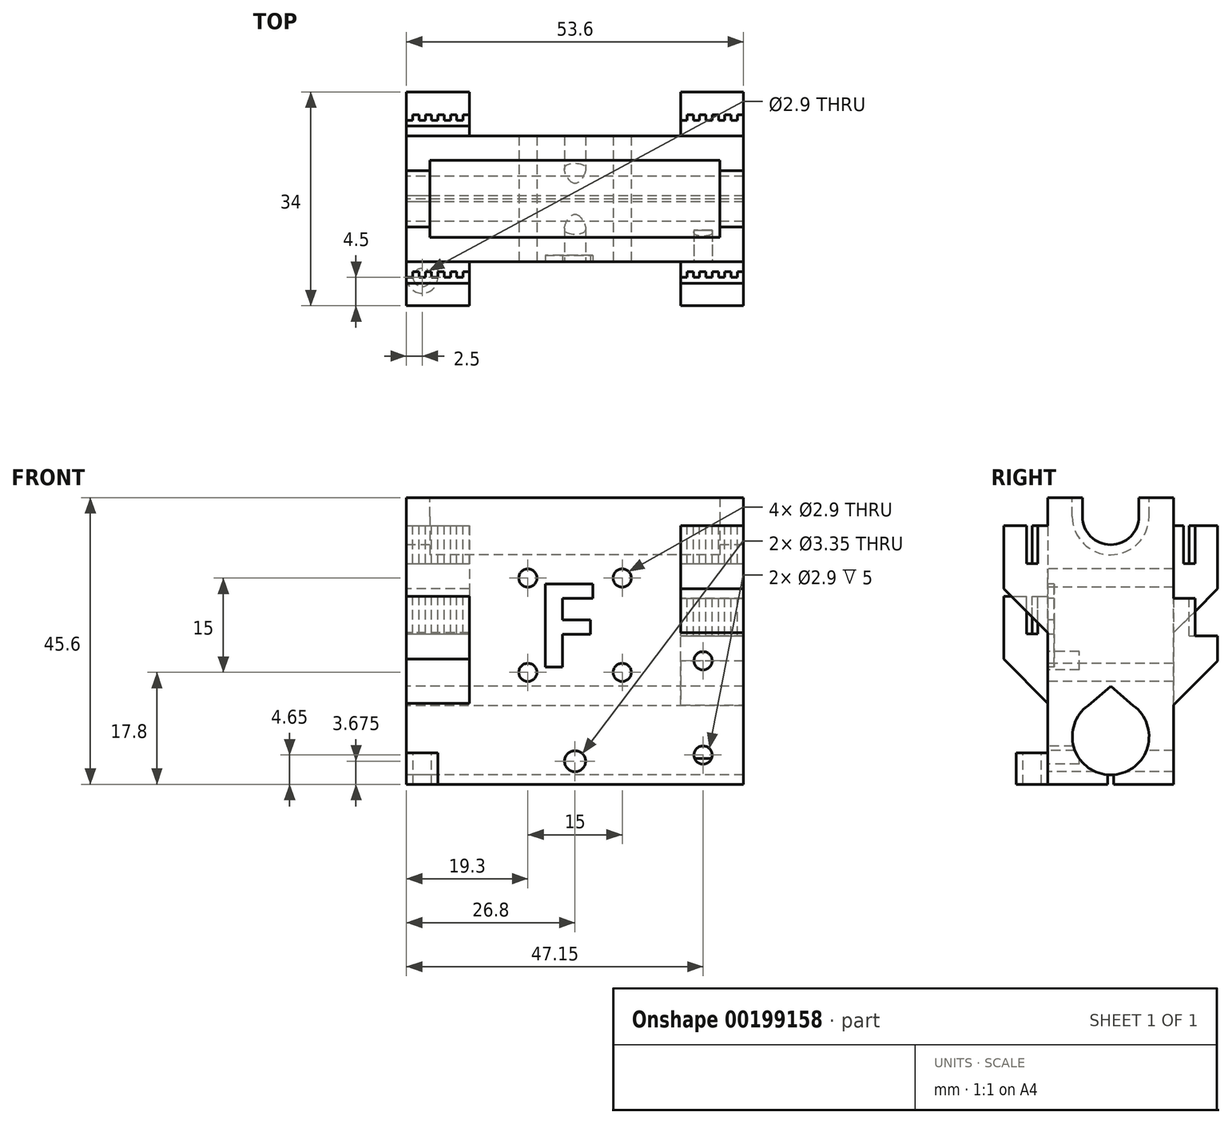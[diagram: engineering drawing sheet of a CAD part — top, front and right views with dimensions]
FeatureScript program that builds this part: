
annotation { "Feature Type Name" : "Feature", "Feature Type Description" : "" }
export const myFeature = defineFeature(function(context is Context, id is Id, definition is map)
    precondition{}
    {
        {
            assignVariable(context, id + "F0", {"name" : "LM8LUU", "anyValue" : 1.8});
        }
        {
            var Q0;
            Q0=qCreatedBy(makeId("Top.planeOp"),FACE);
            var sketch = newSketch(context, id + "F1", { "sketchPlane" : qUnion([Q0])});
            skLineSegment(sketch, "E0.bottom", {"start": v(0, 0) * mm, "end": v(53.6, 0) * mm});
            skLineSegment(sketch, "E0.top", {"start": v(0, 20) * mm, "end": v(53.6, 20) * mm});
            skLineSegment(sketch, "E0.left", {"start": v(0, 0) * mm, "end": v(0, 20) * mm});
            skLineSegment(sketch, "E0.right", {"start": v(53.6, 0) * mm, "end": v(53.6, 20) * mm});
            skSolve(sketch);
        }
        {
            var Q0;
            Q0=qSketchRegion(id+"F1",true);
            extrude(context, id + "F2", {"entities" : qUnion([Q0]), "depth" : 50.6 * mm});
        }
        {
            var Q0;
            {var subQ0=sQuery(id+"F5.wireOp",EDGE,"b7c4184e-802c-4243-a026-41b5801e035c");var subQ1=sQuery(id+"F5.wireOp",EDGE,"2d033815-d19a-4ada-85c1-b424e2f57677");var subQ2=sQuery(id+"F5.wireOp",EDGE,"E15");var subQ3=sQuery(id+"F5.wireOp",EDGE,"deb4647e-459a-4bd0-b85b-410e59fd364d");var subQ4=sQuery(id+"F5.wireOp",EDGE,"1f1fe5f8-645c-480d-a2d4-7acea15178eb");var subQ5=sQuery(id+"F5.wireOp",EDGE,"E4");var subQ6=sQuery(id+"F1.wireOp",EDGE,"E0.left");Q0=makeQuery(id+"F32.boolean.opBoolean","MERGE",FACE,{"derivedFrom":[makeQuery(id+"F19.boolean.opBoolean","MERGE",FACE,{"derivedFrom":[makeQuery(id+"F12.boolean.opBoolean","MERGE",FACE,{"derivedFrom":[makeQuery(id+"F10.boolean.opBoolean","MERGE",FACE,{"derivedFrom":[makeQuery(id+"F8.boolean.opBoolean","MERGE",FACE,{"derivedFrom":[makeQuery(id+"F2.opExtrude","SWEPT_FACE",FACE,{"disambiguationData":[OSD([subQ6])]}),makeQuery(id+"F8.opExtrude","CAP_FACE",FACE,{"disambiguationData":[OSD([subQ6,subQ5,subQ4,subQ3,subQ2,subQ1,subQ0])],"isStart":true})]}),makeQuery(id+"F10.opExtrude","CAP_FACE",FACE,{"disambiguationData":[OSD([subQ6,subQ5,subQ4,subQ3,subQ2,subQ1,subQ0])],"isStart":true})]}),makeQuery(id+"F12.opExtrude","SWEPT_FACE",FACE,{"disambiguationData":[OSD([sQuery(id+"F11.wireOp",EDGE,"E20.left")])]})]}),makeQuery(id+"F19.opExtrude","SWEPT_FACE",FACE,{"disambiguationData":[OSD([sQuery(id+"F18.wireOp",EDGE,"E76.left")])]})]}),makeQuery(id+"F32.opExtrude","SWEPT_FACE",FACE,{"disambiguationData":[OSD([sQuery(id+"F31.wireOp",EDGE,"E147.left")])]})]});}
            var sketch = newSketch(context, id + "F3", { "sketchPlane" : qUnion([Q0])});
            skPoint(sketch, "E1", {"position": v(-20, 45.6) * mm});
            skLineSegment(sketch, "E2.bottom", {"start": v(-20, 45.6) * mm, "end": v(0, 45.6) * mm});
            skLineSegment(sketch, "E2.top", {"start": v(-20, 50.6) * mm, "end": v(0, 50.6) * mm});
            skLineSegment(sketch, "E2.left", {"start": v(-20, 45.6) * mm, "end": v(-20, 50.6) * mm});
            skLineSegment(sketch, "E2.right", {"start": v(0, 45.6) * mm, "end": v(0, 50.6) * mm});
            skSolve(sketch);
        }
        {
            var Q0;
            Q0 = qSketchRegion(id + "F3", true);
            extrude(context, id + "F4", {"entities" : qUnion([Q0]), "operationType" : NewBodyOperationType.REMOVE, "endBound" : BoundingType.THROUGH_ALL, "oppositeDirection" : true, "depth" : 25 * mm});
        }
        {
            var Q0;
            Q0=makeQuery(id+"F2.opExtrude","SWEPT_FACE",FACE,{"disambiguationData":[OSD([sQuery(id+"F1.wireOp",EDGE,"E0.left")])]});
            var sketch = newSketch(context, id + "F5", { "sketchPlane" : qUnion([Q0])});
            skCircle(sketch, "E3", {"center": v(-10, 7.6) * mm, "radius": 6.1 * mm});
            skCircle(sketch, "E4", {"center": v(-10, 42.6) * mm, "radius": 4.5 * mm});
            skLineSegment(sketch, "E5", {"start": v(-20, 7.6) * mm, "end": v(0, 7.6) * mm, "construction": true});
            skLineSegment(sketch, "E6", {"start": v(-10, 7.6) * mm, "end": v(-10, 0) * mm, "construction": true});
            skLineSegment(sketch, "E7", {"start": v(-10, 0) * mm, "end": v(-10.5, 0) * mm});
            skLineSegment(sketch, "E8", {"start": v(-10.5, 0) * mm, "end": v(-10.5, 1.52) * mm});
            skLineSegment(sketch, "E9", {"start": v(-10.5, 1.52) * mm, "end": v(-9.5, 1.52) * mm});
            skLineSegment(sketch, "E10", {"start": v(-9.5, 1.52) * mm, "end": v(-9.5, 0) * mm});
            skLineSegment(sketch, "E11", {"start": v(-9.5, 0) * mm, "end": v(-10, 0) * mm});
            skLineSegment(sketch, "E12", {"start": v(-10, 13.7) * mm, "end": v(-10, 15.6) * mm});
            skLineSegment(sketch, "E13", {"start": v(-10, 15.6) * mm, "end": v(-6.39, 12.51) * mm});
            skLineSegment(sketch, "E14", {"start": v(-10, 15.6) * mm, "end": v(-13.61, 12.51) * mm});
            skCircle(sketch, "E15", {"center": v(-10, 42.6) * mm, "radius": 6.1 * mm});
            skLineSegment(sketch, "E16", {"start": v(-14.5, 42.6) * mm, "end": v(-14.5, 45.6) * mm});
            skLineSegment(sketch, "E17", {"start": v(-16.1, 42.6) * mm, "end": v(-16.1, 45.6) * mm});
            skLineSegment(sketch, "E18", {"start": v(-5.5, 42.6) * mm, "end": v(-5.5, 45.6) * mm});
            skLineSegment(sketch, "E19", {"start": v(-3.9, 42.6) * mm, "end": v(-3.9, 45.6) * mm});
            skSolve(sketch);
        }
        {
            var Q0;
            {var subQ0=sQuery(id+"F5.wireOp",EDGE,"E13");var subQ1=sQuery(id+"F5.wireOp",EDGE,"E3");var subQ3=makeQuery(id+"F5.imprint","INTERSECT",VERTEX,{"disambiguationData":[OD(0.0)],"derivedFrom":[subQ1,subQ0]});Q0=makeQuery(id+"F5.imprint","IMPRINT",FACE,{"disambiguationData":[TD([[makeQuery(id+"F5.imprint","IMPRINT",EDGE,{"disambiguationData":[TD([[subQ3,-1.0]])],"derivedFrom":subQ1}),1.0]])]});}
            var Q1;
            {var subQ0=sQuery(id+"F5.wireOp",EDGE,"E14");var subQ1=sQuery(id+"F5.wireOp",EDGE,"E3");var subQ3=makeQuery(id+"F5.imprint","INTERSECT",VERTEX,{"disambiguationData":[OD(0.0)],"derivedFrom":[subQ1,subQ0]});Q1=makeQuery(id+"F5.imprint","IMPRINT",FACE,{"disambiguationData":[TD([[makeQuery(id+"F5.imprint","IMPRINT",EDGE,{"disambiguationData":[TD([[subQ3,1.0]])],"derivedFrom":subQ1}),1.0]])]});}
            var Q2;
            Q2=makeQuery(id+"F5.imprint","IMPRINT",FACE,{"disambiguationData":[TD([[makeQuery(id+"F5.imprint","IMPRINT",EDGE,{"derivedFrom":sQuery(id+"F5.wireOp",EDGE,"E7")}),-1.0]])]});
            var Q3;
            {var subQ0=sQuery(id+"F5.wireOp",EDGE,"E9");Q3=makeQuery(id+"F5.imprint","IMPRINT",FACE,{"disambiguationData":[TD([[makeQuery(id+"F5.imprint","IMPRINT",EDGE,{"derivedFrom":subQ0}),-1.0]])]});}
            var Q4;
            {var subQ3=sQuery(id+"F5.wireOp",EDGE,"E12");Q4=makeQuery(id+"F5.imprint","IMPRINT",FACE,{"disambiguationData":[TD([[makeQuery(id+"F5.imprint","IMPRINT",EDGE,{"derivedFrom":subQ3}),-1.0]])]});}
            var Q5;
            {var subQ3=sQuery(id+"F5.wireOp",EDGE,"E12");Q5=makeQuery(id+"F5.imprint","IMPRINT",FACE,{"disambiguationData":[TD([[makeQuery(id+"F5.imprint","IMPRINT",EDGE,{"derivedFrom":subQ3}),1.0]])]});}
            var Q6;
            {var subQ7=sQuery(id+"F5.wireOp",EDGE,"E9");Q6=makeQuery(id+"F5.imprint","IMPRINT",FACE,{"disambiguationData":[TD([[makeQuery(id+"F5.imprint","IMPRINT",EDGE,{"derivedFrom":subQ7}),1.0]])]});}
            var Q7;
            {var subQ3=sQuery(id+"F5.wireOp",EDGE,"deb4647e-459a-4bd0-b85b-410e59fd364d");Q7=makeQuery(id+"F5.imprint","IMPRINT",FACE,{"disambiguationData":[TD([[makeQuery(id+"F5.imprint","IMPRINT",EDGE,{"derivedFrom":subQ3}),-1.0]])]});}
            var Q8;
            {var subQ0=sQuery(id+"F5.wireOp",EDGE,"1f1fe5f8-645c-480d-a2d4-7acea15178eb");Q8=makeQuery(id+"F5.imprint","IMPRINT",FACE,{"disambiguationData":[TD([[makeQuery(id+"F5.imprint","IMPRINT",EDGE,{"derivedFrom":subQ0}),1.0]])]});}
            var Q9;
            {var subQ0=sQuery(id+"F5.wireOp",EDGE,"1f1fe5f8-645c-480d-a2d4-7acea15178eb");Q9=makeQuery(id+"F5.imprint","IMPRINT",FACE,{"disambiguationData":[TD([[makeQuery(id+"F5.imprint","IMPRINT",EDGE,{"derivedFrom":subQ0}),1.0]])]});}
            var Q10;
            {var subQ3=sQuery(id+"F5.wireOp",EDGE,"deb4647e-459a-4bd0-b85b-410e59fd364d");Q10=makeQuery(id+"F5.imprint","IMPRINT",FACE,{"disambiguationData":[TD([[makeQuery(id+"F5.imprint","IMPRINT",EDGE,{"derivedFrom":subQ3}),-1.0]])]});}
            var Q11;
            {var subQ1=sQuery(id+"F5.wireOp",EDGE,"E4");var subQ4=makeQuery(id+"F5.imprint","INTERSECT",VERTEX,{"derivedFrom":[subQ1,sQuery(id+"F5.wireOp",EDGE,"deb4647e-459a-4bd0-b85b-410e59fd364d")]});Q11=makeQuery(id+"F5.imprint","IMPRINT",FACE,{"disambiguationData":[TD([[makeQuery(id+"F5.imprint","IMPRINT",EDGE,{"disambiguationData":[TD([[subQ4,-1.0]])],"derivedFrom":subQ1}),1.0]])]});}
            var Q12;
            {var subQ0=sQuery(id+"F5.wireOp",EDGE,"E18");Q12=makeQuery(id+"F5.imprint","IMPRINT",FACE,{"disambiguationData":[TD([[makeQuery(id+"F5.imprint","IMPRINT",EDGE,{"derivedFrom":subQ0}),1.0]])]});}
            var Q13;
            {var subQ0=sQuery(id+"F5.wireOp",EDGE,"E16");Q13=makeQuery(id+"F5.imprint","IMPRINT",FACE,{"disambiguationData":[TD([[makeQuery(id+"F5.imprint","IMPRINT",EDGE,{"derivedFrom":subQ0}),-1.0]])]});}
            extrude(context, id + "F6", {"entities" : qUnion([Q0, Q1, Q2, Q3, Q4, Q5, Q6, Q7, Q8, Q9, Q10, Q11, Q12, Q13]), "operationType" : NewBodyOperationType.REMOVE, "endBound" : BoundingType.THROUGH_ALL, "oppositeDirection" : true, "depth" : 25 * mm});
        }
        {
            var Q0;
            {var subQ0=sQuery(id+"F5.wireOp",EDGE,"E9");Q0=makeQuery(id+"F5.imprint","IMPRINT",FACE,{"disambiguationData":[TD([[makeQuery(id+"F5.imprint","IMPRINT",EDGE,{"derivedFrom":subQ0}),-1.0]])]});}
            var Q1;
            {var subQ0=sQuery(id+"F5.wireOp",EDGE,"E18");Q1=makeQuery(id+"F5.imprint","IMPRINT",FACE,{"disambiguationData":[TD([[makeQuery(id+"F5.imprint","IMPRINT",EDGE,{"derivedFrom":subQ0}),1.0]])]});}
            var Q2;
            {var subQ0=sQuery(id+"F5.wireOp",EDGE,"E16");Q2=makeQuery(id+"F5.imprint","IMPRINT",FACE,{"disambiguationData":[TD([[makeQuery(id+"F5.imprint","IMPRINT",EDGE,{"derivedFrom":subQ0}),-1.0]])]});}
            var Q3;
            {var subQ6=sQuery(id+"F5.wireOp",EDGE,"E16");Q3=makeQuery(id+"F5.imprint","IMPRINT",FACE,{"disambiguationData":[TD([[makeQuery(id+"F5.imprint","IMPRINT",EDGE,{"derivedFrom":subQ6}),1.0]])]});}
            var Q4;
            {var subQ0=makeQuery(id+"F4.boolean.opBoolean","COPY",EDGE,{"derivedFrom":makeQuery(id+"F4.opExtrude","CAP_EDGE",EDGE,{"disambiguationData":[OSD([sQuery(id+"F3.wireOp",EDGE,"E2.bottom")])],"isStart":true})});var subQ2=sQuery(id+"F5.wireOp",EDGE,"E4");var subQ8=makeQuery(id+"F5.imprint","INTERSECT",VERTEX,{"disambiguationData":[OD(0.0)],"derivedFrom":[subQ0,subQ2]});Q4=makeQuery(id+"F5.imprint","IMPRINT",FACE,{"disambiguationData":[TD([[makeQuery(id+"F5.imprint","IMPRINT",EDGE,{"disambiguationData":[TD([[subQ8,-1.0]])],"derivedFrom":subQ2}),-1.0]])]});}
            var Q5;
            {var subQ0=sQuery(id+"F5.wireOp",EDGE,"E19");Q5=makeQuery(id+"F5.imprint","IMPRINT",FACE,{"disambiguationData":[TD([[makeQuery(id+"F5.imprint","IMPRINT",EDGE,{"derivedFrom":subQ0}),1.0]])]});}
            var Q6;
            {var subQ0=sQuery(id+"F5.wireOp",EDGE,"E17");Q6=makeQuery(id+"F5.imprint","IMPRINT",FACE,{"disambiguationData":[TD([[makeQuery(id+"F5.imprint","IMPRINT",EDGE,{"derivedFrom":subQ0}),-1.0]])]});}
            extrude(context, id + "F7", {"entities" : qUnion([Q0, Q1, Q2, Q3, Q4, Q5, Q6]), "operationType" : NewBodyOperationType.REMOVE, "oppositeDirection" : true, "depth" : (46.25 + getVariable(context, 'LM8LUU') * 2) * mm});
        }
        {
            var Q0;
            {var subQ0=sQuery(id+"F5.wireOp",EDGE,"E9");Q0=makeQuery(id+"F5.imprint","IMPRINT",FACE,{"disambiguationData":[TD([[makeQuery(id+"F5.imprint","IMPRINT",EDGE,{"derivedFrom":subQ0}),-1.0]])]});}
            var Q1;
            {var subQ6=sQuery(id+"F5.wireOp",EDGE,"E16");Q1=makeQuery(id+"F5.imprint","IMPRINT",FACE,{"disambiguationData":[TD([[makeQuery(id+"F5.imprint","IMPRINT",EDGE,{"derivedFrom":subQ6}),1.0]])]});}
            var Q2;
            {var subQ0=sQuery(id+"F5.wireOp",EDGE,"E17");Q2=makeQuery(id+"F5.imprint","IMPRINT",FACE,{"disambiguationData":[TD([[makeQuery(id+"F5.imprint","IMPRINT",EDGE,{"derivedFrom":subQ0}),-1.0]])]});}
            var Q3;
            {var subQ0=sQuery(id+"F5.wireOp",EDGE,"E19");Q3=makeQuery(id+"F5.imprint","IMPRINT",FACE,{"disambiguationData":[TD([[makeQuery(id+"F5.imprint","IMPRINT",EDGE,{"derivedFrom":subQ0}),1.0]])]});}
            extrude(context, id + "F8", {"entities" : qUnion([Q0, Q1, Q2, Q3]), "operationType" : NewBodyOperationType.ADD, "oppositeDirection" : true, "depth" : (26.75 - getVariable(context, 'LM8LUU')) * mm});
        }
        {
            var Q0;
            Q0=makeQuery(id+"F5.imprint","IMPRINT",FACE,{"disambiguationData":[TD([[makeQuery(id+"F5.imprint","IMPRINT",EDGE,{"derivedFrom":sQuery(id+"F5.wireOp",EDGE,"E7")}),-1.0]])]});
            var Q1;
            {var subQ0=sQuery(id+"F5.wireOp",EDGE,"E9");Q1=makeQuery(id+"F5.imprint","IMPRINT",FACE,{"disambiguationData":[TD([[makeQuery(id+"F5.imprint","IMPRINT",EDGE,{"derivedFrom":subQ0}),-1.0]])]});}
            var Q2;
            {var subQ0=sQuery(id+"F5.wireOp",EDGE,"E12");Q2=makeQuery(id+"F5.imprint","IMPRINT",FACE,{"disambiguationData":[TD([[makeQuery(id+"F5.imprint","IMPRINT",EDGE,{"derivedFrom":subQ0}),-1.0]])]});}
            var Q3;
            {var subQ0=sQuery(id+"F5.wireOp",EDGE,"E12");Q3=makeQuery(id+"F5.imprint","IMPRINT",FACE,{"disambiguationData":[TD([[makeQuery(id+"F5.imprint","IMPRINT",EDGE,{"derivedFrom":subQ0}),1.0]])]});}
            var Q4;
            {var subQ3=sQuery(id+"F5.wireOp",EDGE,"E9");Q4=makeQuery(id+"F5.imprint","IMPRINT",FACE,{"disambiguationData":[TD([[makeQuery(id+"F5.imprint","IMPRINT",EDGE,{"derivedFrom":subQ3}),1.0]])]});}
            var Q5;
            {var subQ6=sQuery(id+"F5.wireOp",EDGE,"E16");Q5=makeQuery(id+"F5.imprint","IMPRINT",FACE,{"disambiguationData":[TD([[makeQuery(id+"F5.imprint","IMPRINT",EDGE,{"derivedFrom":subQ6}),1.0]])]});}
            var Q6;
            {var subQ0=sQuery(id+"F5.wireOp",EDGE,"E17");Q6=makeQuery(id+"F5.imprint","IMPRINT",FACE,{"disambiguationData":[TD([[makeQuery(id+"F5.imprint","IMPRINT",EDGE,{"derivedFrom":subQ0}),-1.0]])]});}
            var Q7;
            {var subQ0=sQuery(id+"F5.wireOp",EDGE,"E19");Q7=makeQuery(id+"F5.imprint","IMPRINT",FACE,{"disambiguationData":[TD([[makeQuery(id+"F5.imprint","IMPRINT",EDGE,{"derivedFrom":subQ0}),1.0]])]});}
            extrude(context, id + "F9", {"entities" : qUnion([Q0, Q1, Q2, Q3, Q4, Q5, Q6, Q7]), "operationType" : NewBodyOperationType.REMOVE, "oppositeDirection" : true, "depth" : (23.25 + getVariable(context, 'LM8LUU')) * mm});
        }
        {
            var Q0;
            {var subQ0=sQuery(id+"F5.wireOp",EDGE,"E9");Q0=makeQuery(id+"F5.imprint","IMPRINT",FACE,{"disambiguationData":[TD([[makeQuery(id+"F5.imprint","IMPRINT",EDGE,{"derivedFrom":subQ0}),-1.0]])]});}
            var Q1;
            {var subQ6=sQuery(id+"F5.wireOp",EDGE,"E16");Q1=makeQuery(id+"F5.imprint","IMPRINT",FACE,{"disambiguationData":[TD([[makeQuery(id+"F5.imprint","IMPRINT",EDGE,{"derivedFrom":subQ6}),1.0]])]});}
            var Q2;
            {var subQ0=sQuery(id+"F5.wireOp",EDGE,"E17");Q2=makeQuery(id+"F5.imprint","IMPRINT",FACE,{"disambiguationData":[TD([[makeQuery(id+"F5.imprint","IMPRINT",EDGE,{"derivedFrom":subQ0}),-1.0]])]});}
            var Q3;
            {var subQ0=sQuery(id+"F5.wireOp",EDGE,"E19");Q3=makeQuery(id+"F5.imprint","IMPRINT",FACE,{"disambiguationData":[TD([[makeQuery(id+"F5.imprint","IMPRINT",EDGE,{"derivedFrom":subQ0}),1.0]])]});}
            extrude(context, id + "F10", {"entities" : qUnion([Q0, Q1, Q2, Q3]), "operationType" : NewBodyOperationType.ADD, "oppositeDirection" : true, "depth" : 3.75 * mm});
        }
        {
            var Q0;
            Q0=makeQuery(id+"F2.opExtrude","SWEPT_FACE",FACE,{"disambiguationData":[OSD([sQuery(id+"F1.wireOp",EDGE,"E0.bottom")])]});
            var sketch = newSketch(context, id + "F11", { "sketchPlane" : qUnion([Q0])});
            skLineSegment(sketch, "E20.bottom", {"start": v(0, 29.9) * mm, "end": v(10, 29.9) * mm});
            skLineSegment(sketch, "E20.top", {"start": v(0, 9.9) * mm, "end": v(10, 9.9) * mm});
            skLineSegment(sketch, "E20.left", {"start": v(0, 29.9) * mm, "end": v(0, 9.9) * mm});
            skLineSegment(sketch, "E20.right", {"start": v(10, 29.9) * mm, "end": v(10, 9.9) * mm});
            skLineSegment(sketch, "E21.bottom", {"start": v(53.6, 41.1) * mm, "end": v(43.6, 41.1) * mm});
            skLineSegment(sketch, "E21.top", {"start": v(53.6, 21.1) * mm, "end": v(43.6, 21.1) * mm});
            skLineSegment(sketch, "E21.left", {"start": v(53.6, 41.1) * mm, "end": v(53.6, 21.1) * mm});
            skLineSegment(sketch, "E21.right", {"start": v(43.6, 41.1) * mm, "end": v(43.6, 21.1) * mm});
            skPoint(sketch, "E22", {"position": v(0, 47.6) * mm});
            skPoint(sketch, "E23", {"position": v(0, 9.4) * mm});
            skSolve(sketch);
        }
        {
            var Q0;
            Q0=qSketchRegion(id+"F11",true);
            extrude(context, id + "F12", {"entities" : qUnion([Q0]), "operationType" : NewBodyOperationType.ADD, "depth" : 7 * mm});
        }
        {
            var Q0;
            Q0=makeQuery(id+"F12.opExtrude","CAP_EDGE",EDGE,{"disambiguationData":[OSD([sQuery(id+"F11.wireOp",EDGE,"E20.top")])],"isStart":false});
            var Q1;
            Q1=makeQuery(id+"F12.opExtrude","CAP_EDGE",EDGE,{"disambiguationData":[OSD([sQuery(id+"F11.wireOp",EDGE,"E21.top")])],"isStart":false});
            chamfer(context, id + "F13", {"entities" : qUnion([Q0, Q1]), "width" : 10 * mm, "tangentPropagation" : true});
        }
        {
            var Q0;
            Q0=makeQuery(id+"F12.opExtrude","SWEPT_FACE",FACE,{"disambiguationData":[OSD([sQuery(id+"F11.wireOp",EDGE,"E20.bottom")])]});
            var sketch = newSketch(context, id + "F14", { "sketchPlane" : qUnion([Q0])});
            skLineSegment(sketch, "E24", {"start": v(-935.9, 0) * mm, "end": v(-935.88, -4.54) * mm});
            skLineSegment(sketch, "E25.left", {"start": v(0, -3.4) * mm, "end": v(0, -1.6) * mm});
            skLineSegment(sketch, "E26", {"start": v(6, -2.5) * mm, "end": v(7, -2.5) * mm});
            skLineSegment(sketch, "E27", {"start": v(4, -2.5) * mm, "end": v(5, -2.5) * mm});
            skLineSegment(sketch, "E28", {"start": v(0, -2.5) * mm, "end": v(1, -2.5) * mm});
            skLineSegment(sketch, "E29", {"start": v(7, -1.6) * mm, "end": v(8, -1.6) * mm});
            skLineSegment(sketch, "E30", {"start": v(2, -2.5) * mm, "end": v(3, -2.5) * mm});
            skLineSegment(sketch, "E31", {"start": v(3, -1.6) * mm, "end": v(4, -1.6) * mm});
            skLineSegment(sketch, "E32", {"start": v(8, -2.5) * mm, "end": v(9, -2.5) * mm});
            skLineSegment(sketch, "E33", {"start": v(8, -1.6) * mm, "end": v(8, -2.5) * mm});
            skLineSegment(sketch, "E34", {"start": v(9, -2.5) * mm, "end": v(9, -1.6) * mm});
            skLineSegment(sketch, "E35", {"start": v(10, -1.6) * mm, "end": v(10, -2.5) * mm});
            skLineSegment(sketch, "E36", {"start": v(6, -1.6) * mm, "end": v(6, -2.5) * mm});
            skLineSegment(sketch, "E37", {"start": v(2, -1.6) * mm, "end": v(2, -2.5) * mm});
            skLineSegment(sketch, "E38", {"start": v(1, -1.6) * mm, "end": v(2, -1.6) * mm});
            skLineSegment(sketch, "E39", {"start": v(1, -2.5) * mm, "end": v(1, -1.6) * mm});
            skLineSegment(sketch, "E40", {"start": v(9, -1.6) * mm, "end": v(10, -1.6) * mm});
            skLineSegment(sketch, "E41", {"start": v(5, -1.6) * mm, "end": v(6, -1.6) * mm});
            skLineSegment(sketch, "E42", {"start": v(5, -2.5) * mm, "end": v(5, -1.6) * mm});
            skLineSegment(sketch, "E43", {"start": v(3, -2.5) * mm, "end": v(3, -1.6) * mm});
            skLineSegment(sketch, "E44", {"start": v(4, -1.6) * mm, "end": v(4, -2.5) * mm});
            skLineSegment(sketch, "E45", {"start": v(7, -2.5) * mm, "end": v(7, -1.6) * mm});
            skLineSegment(sketch, "E46", {"start": v(0, -1.6) * mm, "end": v(0, -2.5) * mm});
            skLineSegment(sketch, "E47", {"start": v(10, -2.5) * mm, "end": v(10, -3.4) * mm});
            skLineSegment(sketch, "E48", {"start": v(0, -3.4) * mm, "end": v(10, -3.4) * mm});
            skLineSegment(sketch, "E49", {"start": v(5.3, -1.6) * mm, "end": v(5.3, 0) * mm});
            skSolve(sketch);
        }
        {
            var Q0;
            Q0=qSketchRegion(id+"F14",true);
            extrude(context, id + "F15", {"entities" : qUnion([Q0]), "operationType" : NewBodyOperationType.REMOVE, "oppositeDirection" : true, "depth" : 6 * mm});
        }
        {
            var Q0;
            Q0=makeQuery(id+"F12.opExtrude","SWEPT_FACE",FACE,{"disambiguationData":[OSD([sQuery(id+"F11.wireOp",EDGE,"E21.bottom")])]});
            var sketch = newSketch(context, id + "F16", { "sketchPlane" : qUnion([Q0])});
            skLineSegment(sketch, "E50.left", {"start": v(43.6, -3.4) * mm, "end": v(43.6, -1.6) * mm});
            skLineSegment(sketch, "E51", {"start": v(49.6, -2.5) * mm, "end": v(50.6, -2.5) * mm});
            skLineSegment(sketch, "E52", {"start": v(47.6, -2.5) * mm, "end": v(48.6, -2.5) * mm});
            skLineSegment(sketch, "E53", {"start": v(43.6, -2.5) * mm, "end": v(44.6, -2.5) * mm});
            skLineSegment(sketch, "E54", {"start": v(50.6, -1.6) * mm, "end": v(51.6, -1.6) * mm});
            skLineSegment(sketch, "E55", {"start": v(45.6, -2.5) * mm, "end": v(46.6, -2.5) * mm});
            skLineSegment(sketch, "E56", {"start": v(46.6, -1.6) * mm, "end": v(47.6, -1.6) * mm});
            skLineSegment(sketch, "E57", {"start": v(51.6, -2.5) * mm, "end": v(52.6, -2.5) * mm});
            skLineSegment(sketch, "E58", {"start": v(51.6, -1.6) * mm, "end": v(51.6, -2.5) * mm});
            skLineSegment(sketch, "E59", {"start": v(52.6, -2.5) * mm, "end": v(52.6, -1.6) * mm});
            skLineSegment(sketch, "E60", {"start": v(53.6, -1.6) * mm, "end": v(53.6, -2.5) * mm});
            skLineSegment(sketch, "E61", {"start": v(49.6, -1.6) * mm, "end": v(49.6, -2.5) * mm});
            skLineSegment(sketch, "E62", {"start": v(45.6, -1.6) * mm, "end": v(45.6, -2.5) * mm});
            skLineSegment(sketch, "E63", {"start": v(44.6, -1.6) * mm, "end": v(45.6, -1.6) * mm});
            skLineSegment(sketch, "E64", {"start": v(44.6, -2.5) * mm, "end": v(44.6, -1.6) * mm});
            skLineSegment(sketch, "E65", {"start": v(52.6, -1.6) * mm, "end": v(53.6, -1.6) * mm});
            skLineSegment(sketch, "E66", {"start": v(48.6, -1.6) * mm, "end": v(49.6, -1.6) * mm});
            skLineSegment(sketch, "E67", {"start": v(48.6, -2.5) * mm, "end": v(48.6, -1.6) * mm});
            skLineSegment(sketch, "E68", {"start": v(46.6, -2.5) * mm, "end": v(46.6, -1.6) * mm});
            skLineSegment(sketch, "E69", {"start": v(47.6, -1.6) * mm, "end": v(47.6, -2.5) * mm});
            skLineSegment(sketch, "E70", {"start": v(50.6, -2.5) * mm, "end": v(50.6, -1.6) * mm});
            skLineSegment(sketch, "E71", {"start": v(43.6, -1.6) * mm, "end": v(43.6, -2.5) * mm});
            skLineSegment(sketch, "E72", {"start": v(53.6, -2.5) * mm, "end": v(53.6, -3.4) * mm});
            skLineSegment(sketch, "E73", {"start": v(43.6, -3.4) * mm, "end": v(53.6, -3.4) * mm});
            skLineSegment(sketch, "E74", {"start": v(48.83, -1.6) * mm, "end": v(48.83, 0) * mm});
            skSolve(sketch);
        }
        {
            var Q0;
            Q0=qSketchRegion(id+"F16",true);
            extrude(context, id + "F17", {"entities" : qUnion([Q0]), "operationType" : NewBodyOperationType.REMOVE, "oppositeDirection" : true, "depth" : 6 * mm});
        }
        {
            var Q0;
            Q0=makeQuery(id+"F2.opExtrude","SWEPT_FACE",FACE,{"disambiguationData":[OSD([sQuery(id+"F1.wireOp",EDGE,"E0.top")])]});
            var sketch = newSketch(context, id + "F18", { "sketchPlane" : qUnion([Q0])});
            skLineSegment(sketch, "E75.bottom", {"start": v(-53.6, 9.6) * mm, "end": v(-43.6, 9.6) * mm});
            skLineSegment(sketch, "E75.top", {"start": v(-53.6, 29.6) * mm, "end": v(-43.6, 29.6) * mm});
            skLineSegment(sketch, "E75.left", {"start": v(-53.6, 9.6) * mm, "end": v(-53.6, 29.6) * mm});
            skLineSegment(sketch, "E75.right", {"start": v(-43.6, 9.6) * mm, "end": v(-43.6, 29.6) * mm});
            skLineSegment(sketch, "E76.bottom", {"start": v(0, 41.1) * mm, "end": v(-10, 41.1) * mm});
            skLineSegment(sketch, "E76.top", {"start": v(0, 21.1) * mm, "end": v(-10, 21.1) * mm});
            skLineSegment(sketch, "E76.left", {"start": v(0, 41.1) * mm, "end": v(0, 21.1) * mm});
            skLineSegment(sketch, "E76.right", {"start": v(-10, 41.1) * mm, "end": v(-10, 21.1) * mm});
            skSolve(sketch);
        }
        {
            var Q0;
            Q0=qSketchRegion(id+"F18",true);
            extrude(context, id + "F19", {"entities" : qUnion([Q0]), "operationType" : NewBodyOperationType.ADD, "depth" : 7 * mm});
        }
        {
            var Q0;
            Q0=makeQuery(id+"F19.opExtrude","SWEPT_FACE",FACE,{"disambiguationData":[OSD([sQuery(id+"F18.wireOp",EDGE,"E75.top")])]});
            var sketch = newSketch(context, id + "F20", { "sketchPlane" : qUnion([Q0])});
            skLineSegment(sketch, "E77.left", {"start": v(43.6, 21.6) * mm, "end": v(43.6, 23.4) * mm});
            skLineSegment(sketch, "E78", {"start": v(49.6, 22.5) * mm, "end": v(50.6, 22.5) * mm});
            skLineSegment(sketch, "E79", {"start": v(47.6, 22.5) * mm, "end": v(48.6, 22.5) * mm});
            skLineSegment(sketch, "E80", {"start": v(43.6, 22.5) * mm, "end": v(44.6, 22.5) * mm});
            skLineSegment(sketch, "E81", {"start": v(50.6, 23.4) * mm, "end": v(51.6, 23.4) * mm});
            skLineSegment(sketch, "E82", {"start": v(45.6, 22.5) * mm, "end": v(46.6, 22.5) * mm});
            skLineSegment(sketch, "E83", {"start": v(46.6, 23.4) * mm, "end": v(47.6, 23.4) * mm});
            skLineSegment(sketch, "E84", {"start": v(51.6, 22.5) * mm, "end": v(52.6, 22.5) * mm});
            skLineSegment(sketch, "E85", {"start": v(51.6, 23.4) * mm, "end": v(51.6, 22.5) * mm});
            skLineSegment(sketch, "E86", {"start": v(52.6, 22.5) * mm, "end": v(52.6, 23.4) * mm});
            skLineSegment(sketch, "E87", {"start": v(53.6, 23.4) * mm, "end": v(53.6, 22.5) * mm});
            skLineSegment(sketch, "E88", {"start": v(49.6, 23.4) * mm, "end": v(49.6, 22.5) * mm});
            skLineSegment(sketch, "E89", {"start": v(45.6, 23.4) * mm, "end": v(45.6, 22.5) * mm});
            skLineSegment(sketch, "E90", {"start": v(44.6, 23.4) * mm, "end": v(45.6, 23.4) * mm});
            skLineSegment(sketch, "E91", {"start": v(44.6, 22.5) * mm, "end": v(44.6, 23.4) * mm});
            skLineSegment(sketch, "E92", {"start": v(52.6, 23.4) * mm, "end": v(53.6, 23.4) * mm});
            skLineSegment(sketch, "E93", {"start": v(48.6, 23.4) * mm, "end": v(49.6, 23.4) * mm});
            skLineSegment(sketch, "E94", {"start": v(48.6, 22.5) * mm, "end": v(48.6, 23.4) * mm});
            skLineSegment(sketch, "E95", {"start": v(46.6, 22.5) * mm, "end": v(46.6, 23.4) * mm});
            skLineSegment(sketch, "E96", {"start": v(47.6, 23.4) * mm, "end": v(47.6, 22.5) * mm});
            skLineSegment(sketch, "E97", {"start": v(50.6, 22.5) * mm, "end": v(50.6, 23.4) * mm});
            skLineSegment(sketch, "E98", {"start": v(43.6, 23.4) * mm, "end": v(43.6, 22.5) * mm});
            skLineSegment(sketch, "E99", {"start": v(53.6, 22.5) * mm, "end": v(53.6, 21.6) * mm});
            skLineSegment(sketch, "E100", {"start": v(43.6, 21.6) * mm, "end": v(53.6, 21.6) * mm});
            skLineSegment(sketch, "E101", {"start": v(48.6, 21.6) * mm, "end": v(48.6, 20) * mm});
            skSolve(sketch);
        }
        {
            var Q0;
            {var subQ4=sQuery(id+"F20.wireOp",EDGE,"E77.left");Q0=makeQuery(id+"F20.imprint","IMPRINT",FACE,{"disambiguationData":[TD([[makeQuery(id+"F20.imprint","IMPRINT",EDGE,{"derivedFrom":subQ4}),1.0]])]});}
            extrude(context, id + "F21", {"entities" : qUnion([Q0]), "operationType" : NewBodyOperationType.REMOVE, "oppositeDirection" : true, "depth" : 6 * mm});
        }
        {
            var Q0;
            Q0=makeQuery(id+"F19.opExtrude","SWEPT_FACE",FACE,{"disambiguationData":[OSD([sQuery(id+"F18.wireOp",EDGE,"E76.bottom")])]});
            var sketch = newSketch(context, id + "F22", { "sketchPlane" : qUnion([Q0])});
            skLineSegment(sketch, "E102", {"start": v(6, 22.5) * mm, "end": v(7, 22.5) * mm});
            skLineSegment(sketch, "E103", {"start": v(4, 22.5) * mm, "end": v(5, 22.5) * mm});
            skLineSegment(sketch, "E104", {"start": v(0, 22.5) * mm, "end": v(1, 22.5) * mm});
            skLineSegment(sketch, "E105", {"start": v(7, 23.4) * mm, "end": v(8, 23.4) * mm});
            skLineSegment(sketch, "E106", {"start": v(2, 22.5) * mm, "end": v(3, 22.5) * mm});
            skLineSegment(sketch, "E107", {"start": v(3, 23.4) * mm, "end": v(4, 23.4) * mm});
            skLineSegment(sketch, "E108", {"start": v(8, 22.5) * mm, "end": v(9, 22.5) * mm});
            skLineSegment(sketch, "E109", {"start": v(8, 23.4) * mm, "end": v(8, 22.5) * mm});
            skLineSegment(sketch, "E110", {"start": v(9, 22.5) * mm, "end": v(9, 23.4) * mm});
            skLineSegment(sketch, "E111", {"start": v(10, 23.4) * mm, "end": v(10, 22.5) * mm});
            skLineSegment(sketch, "E112", {"start": v(6, 23.4) * mm, "end": v(6, 22.5) * mm});
            skLineSegment(sketch, "E113", {"start": v(2, 23.4) * mm, "end": v(2, 22.5) * mm});
            skLineSegment(sketch, "E114", {"start": v(1, 23.4) * mm, "end": v(2, 23.4) * mm});
            skLineSegment(sketch, "E115", {"start": v(1, 22.5) * mm, "end": v(1, 23.4) * mm});
            skLineSegment(sketch, "E116", {"start": v(9, 23.4) * mm, "end": v(10, 23.4) * mm});
            skLineSegment(sketch, "E117", {"start": v(5, 23.4) * mm, "end": v(6, 23.4) * mm});
            skLineSegment(sketch, "E118", {"start": v(5, 22.5) * mm, "end": v(5, 23.4) * mm});
            skLineSegment(sketch, "E119", {"start": v(3, 22.5) * mm, "end": v(3, 23.4) * mm});
            skLineSegment(sketch, "E120", {"start": v(4, 23.4) * mm, "end": v(4, 22.5) * mm});
            skLineSegment(sketch, "E121", {"start": v(7, 22.5) * mm, "end": v(7, 23.4) * mm});
            skLineSegment(sketch, "E122", {"start": v(10, 22.5) * mm, "end": v(10, 21.6) * mm});
            skLineSegment(sketch, "E123", {"start": v(0, 21.6) * mm, "end": v(10, 21.6) * mm});
            skLineSegment(sketch, "E124", {"start": v(5, 21.6) * mm, "end": v(5, 20) * mm});
            skLineSegment(sketch, "E125", {"start": v(0, 21.6) * mm, "end": v(0, 22.5) * mm});
            skSolve(sketch);
        }
        {
            var Q0;
            Q0=makeQuery(id+"F22.imprint","IMPRINT",FACE,{"disambiguationData":[TD([[makeQuery(id+"F22.imprint","IMPRINT",EDGE,{"derivedFrom":sQuery(id+"F22.wireOp",EDGE,"E102")}),-1.0]])]});
            extrude(context, id + "F23", {"entities" : qUnion([Q0]), "operationType" : NewBodyOperationType.REMOVE, "oppositeDirection" : true, "depth" : 6 * mm});
        }
        {
            var Q0;
            Q0=makeQuery(id+"F19.opExtrude","CAP_EDGE",EDGE,{"disambiguationData":[OSD([sQuery(id+"F18.wireOp",EDGE,"E76.top")])],"isStart":false});
            var Q1;
            Q1=makeQuery(id+"F19.opExtrude","CAP_EDGE",EDGE,{"disambiguationData":[OSD([sQuery(id+"F18.wireOp",EDGE,"E75.bottom")])],"isStart":false});
            chamfer(context, id + "F24", {"entities" : qUnion([Q0, Q1]), "width" : 10 * mm, "tangentPropagation" : true});
        }
        {
            var Q0;
            Q0=makeQuery(id+"F2.opExtrude","SWEPT_FACE",FACE,{"disambiguationData":[OSD([sQuery(id+"F1.wireOp",EDGE,"E0.bottom")])]});
            var sketch = newSketch(context, id + "F25", { "sketchPlane" : qUnion([Q0])});
            skCircle(sketch, "E126", {"center": v(19.3, 32.8) * mm, "radius": 1.45 * mm});
            skCircle(sketch, "E127", {"center": v(34.3, 32.8) * mm, "radius": 1.45 * mm});
            skCircle(sketch, "E128", {"center": v(19.3, 17.8) * mm, "radius": 1.45 * mm});
            skCircle(sketch, "E129", {"center": v(34.3, 17.8) * mm, "radius": 1.45 * mm});
            skLineSegment(sketch, "E130", {"start": v(19.3, 32.8) * mm, "end": v(0, 32.8) * mm});
            skLineSegment(sketch, "E131", {"start": v(34.3, 17.8) * mm, "end": v(53.6, 17.8) * mm});
            skLineSegment(sketch, "E132", {"start": v(34.3, 32.8) * mm, "end": v(34.3, 50.6) * mm});
            skLineSegment(sketch, "E133", {"start": v(19.3, 17.8) * mm, "end": v(19.3, 0) * mm});
            skCircle(sketch, "E134", {"center": v(26.8, 3.68) * mm, "radius": 1.68 * mm});
            skLineSegment(sketch, "E135", {"start": v(26.8, 0) * mm, "end": v(26.8, 13.82) * mm, "construction": true});
            skSolve(sketch);
        }
        {
            var Q0;
            Q0=qSketchRegion(id+"F25",true);
            var Q1;
            Q1=makeQuery(id+"F25.imprint","IMPRINT",FACE,{"disambiguationData":[TD([[makeQuery(id+"F25.imprint","IMPRINT",EDGE,{"derivedFrom":sQuery(id+"F25.wireOp",EDGE,"E126")}),1.0]])]});
            var Q2;
            Q2=makeQuery(id+"F25.imprint","IMPRINT",FACE,{"disambiguationData":[TD([[makeQuery(id+"F25.imprint","IMPRINT",EDGE,{"derivedFrom":sQuery(id+"F25.wireOp",EDGE,"E127")}),1.0]])]});
            var Q3;
            Q3=makeQuery(id+"F25.imprint","IMPRINT",FACE,{"disambiguationData":[TD([[makeQuery(id+"F25.imprint","IMPRINT",EDGE,{"derivedFrom":sQuery(id+"F25.wireOp",EDGE,"E129")}),1.0]])]});
            var Q4;
            Q4=makeQuery(id+"F25.imprint","IMPRINT",FACE,{"disambiguationData":[TD([[makeQuery(id+"F25.imprint","IMPRINT",EDGE,{"derivedFrom":sQuery(id+"F25.wireOp",EDGE,"E128")}),1.0]])]});
            extrude(context, id + "F26", {"entities" : qUnion([Q0, Q1, Q2, Q3, Q4]), "operationType" : NewBodyOperationType.REMOVE, "endBound" : BoundingType.THROUGH_ALL, "oppositeDirection" : true, "depth" : 25 * mm});
        }
        {
            var Q0;
            Q0=makeQuery(id+"F2.opExtrude","SWEPT_FACE",FACE,{"disambiguationData":[OSD([sQuery(id+"F1.wireOp",EDGE,"E0.bottom")])]});
            var sketch = newSketch(context, id + "F27", { "sketchPlane" : qUnion([Q0])});
            skCircle(sketch, "E136", {"center": v(47.15, 19.65) * mm, "radius": 1.45 * mm});
            skCircle(sketch, "E137", {"center": v(47.15, 4.65) * mm, "radius": 1.45 * mm});
            skSolve(sketch);
        }
        {
            var Q0;
            Q0=qSketchRegion(id+"F27",true);
            extrude(context, id + "F28", {"entities" : qUnion([Q0]), "operationType" : NewBodyOperationType.REMOVE, "oppositeDirection" : true, "depth" : 5 * mm});
        }
        {
            var Q0;
            Q0=makeQuery(id+"F2.opExtrude","SWEPT_FACE",FACE,{"disambiguationData":[OSD([sQuery(id+"F1.wireOp",EDGE,"E0.bottom")])]});
            var sketch = newSketch(context, id + "F29", { "sketchPlane" : qUnion([Q0])});
            skText(sketch, "E138", { "text": "F", "fontName": "OpenSans-Bold.ttf"});
            skLineSegment(sketch, "E139", {"start": v(19.3, 32.8) * mm, "end": v(19.3, 17.8) * mm, "construction": true});
            skLineSegment(sketch, "E140", {"start": v(19.3, 17.8) * mm, "end": v(34.3, 17.8) * mm, "construction": true});
            skLineSegment(sketch, "E141", {"start": v(34.3, 17.8) * mm, "end": v(34.3, 32.8) * mm, "construction": true});
            skLineSegment(sketch, "E142", {"start": v(34.3, 32.8) * mm, "end": v(19.3, 32.8) * mm, "construction": true});
            skLineSegment(sketch, "E143", {"start": v(19.3, 25.3) * mm, "end": v(22.2, 25.3) * mm, "construction": true});
            skLineSegment(sketch, "E144", {"start": v(31.4, 25.3) * mm, "end": v(34.3, 25.3) * mm, "construction": true});
            skLineSegment(sketch, "E145", {"start": v(26.8, 18.66) * mm, "end": v(26.8, 17.8) * mm, "construction": true});
            skLineSegment(sketch, "E146", {"start": v(26.8, 32.8) * mm, "end": v(26.8, 31.94) * mm, "construction": true});
            const initialGuessF29  = {"E138": [0.0204, 0.01866, 1, 0, 0.01328]};
            skSetInitialGuess(sketch, initialGuessF29);
            skSolve(sketch);
        }
        {
            var Q0;
            Q0=qSketchRegion(id+"F29",true);
            extrude(context, id + "F30", {"entities" : qUnion([Q0]), "operationType" : NewBodyOperationType.REMOVE, "oppositeDirection" : true, "depth" : 1 * mm});
        }
        {
            var Q0;
            Q0=makeQuery(id+"F2.opExtrude","SWEPT_FACE",FACE,{"disambiguationData":[OSD([sQuery(id+"F1.wireOp",EDGE,"E0.bottom")])]});
            var sketch = newSketch(context, id + "F31", { "sketchPlane" : qUnion([Q0])});
            skLineSegment(sketch, "E147.bottom", {"start": v(0, 0) * mm, "end": v(5, 0) * mm});
            skLineSegment(sketch, "E147.top", {"start": v(0, 5) * mm, "end": v(5, 5) * mm});
            skLineSegment(sketch, "E147.left", {"start": v(0, 0) * mm, "end": v(0, 5) * mm});
            skLineSegment(sketch, "E147.right", {"start": v(5, 0) * mm, "end": v(5, 5) * mm});
            skSolve(sketch);
        }
        {
            var Q0;
            Q0=qSketchRegion(id+"F31",true);
            extrude(context, id + "F32", {"entities" : qUnion([Q0]), "operationType" : NewBodyOperationType.ADD, "depth" : 5 * mm});
        }
        {
            var Q0;
            Q0=makeQuery(id+"F32.opExtrude","SWEPT_FACE",FACE,{"disambiguationData":[OSD([sQuery(id+"F31.wireOp",EDGE,"E147.top")])]});
            var sketch = newSketch(context, id + "F33", { "sketchPlane" : qUnion([Q0])});
            skCircle(sketch, "E148", {"center": v(2.5, -2.5) * mm, "radius": 1.45 * mm});
            skLineSegment(sketch, "E149", {"start": v(0, -2.5) * mm, "end": v(5, -2.5) * mm});
            skSolve(sketch);
        }
        {
            var Q0;
            Q0=qSketchRegion(id+"F33",true);
            extrude(context, id + "F34", {"entities" : qUnion([Q0]), "operationType" : NewBodyOperationType.REMOVE, "oppositeDirection" : true, "depth" : 25 * mm});
        }
        {
            var Q0;
            Q0=makeQuery(id+"F32.opExtrude","CAP_EDGE",EDGE,{"disambiguationData":[OSD([sQuery(id+"F31.wireOp",EDGE,"E147.left")])],"isStart":false});
            var Q1;
            Q1=makeQuery(id+"F32.opExtrude","CAP_EDGE",EDGE,{"disambiguationData":[OSD([sQuery(id+"F31.wireOp",EDGE,"E147.right")])],"isStart":false});
            fillet(context, id + "F35", {"entities" : qUnion([Q0, Q1]), "radius" : 2.5 * mm, "tangentPropagation" : true, "allowEdgeOverflow" : false});
        }
    });
